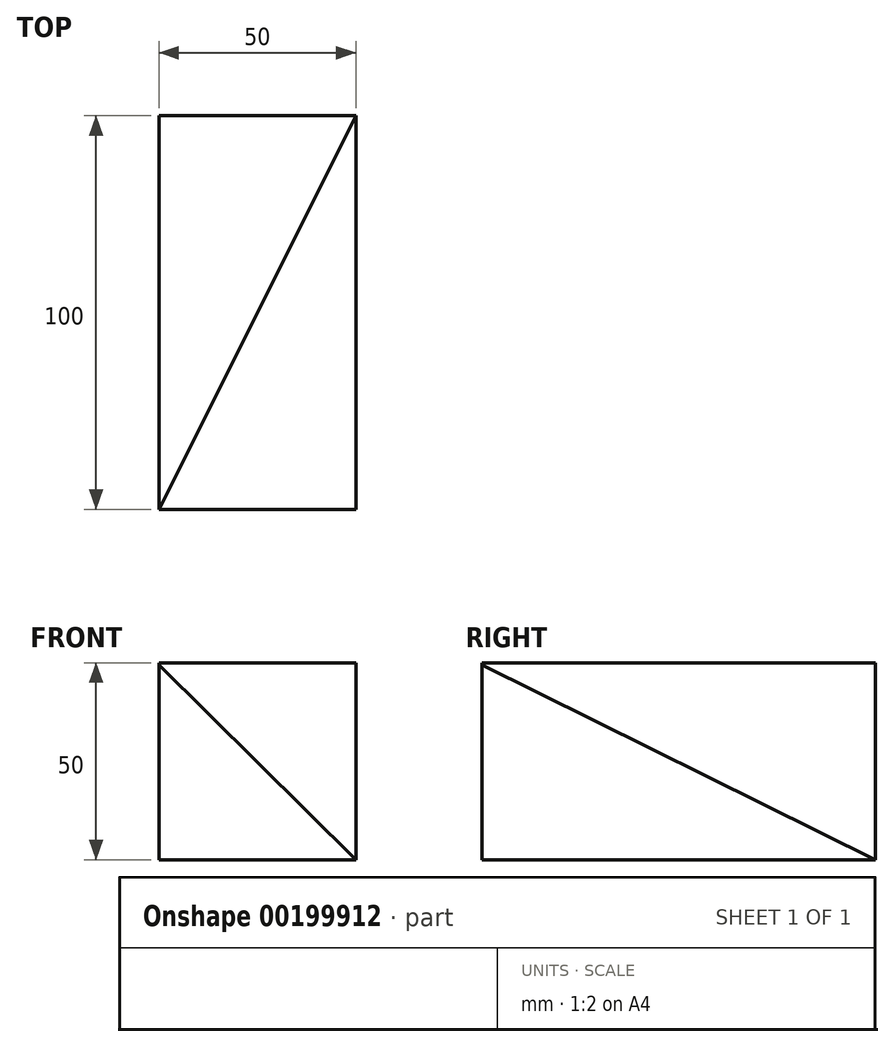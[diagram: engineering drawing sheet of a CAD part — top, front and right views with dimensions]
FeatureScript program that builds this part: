
annotation { "Feature Type Name" : "Feature", "Feature Type Description" : "" }
export const myFeature = defineFeature(function(context is Context, id is Id, definition is map)
    precondition{}
    {
        {
            var Q0;
            Q0=qCreatedBy(makeId("Top.planeOp"),FACE);
            var sketch = newSketch(context, id + "F0", { "sketchPlane" : qUnion([Q0])});
            skLineSegment(sketch, "E0", {"start": v(0, 0) * mm, "end": v(0, 100) * mm});
            skLineSegment(sketch, "E1", {"start": v(0, 100) * mm, "end": v(50, 100) * mm});
            skLineSegment(sketch, "E2", {"start": v(50, 100) * mm, "end": v(0, 0) * mm});
            skSolve(sketch);
        }
        {
            var Q0;
            Q0 = qSketchRegion(id + "F0", true);
            extrude(context, id + "F1", {"entities" : qUnion([Q0]), "depth" : 50 * mm});
        }
        {
            var Q0;
            Q0=qCreatedBy(makeId("Front.planeOp"),FACE);
            var sketch = newSketch(context, id + "F2", { "sketchPlane" : qUnion([Q0])});
            skLineSegment(sketch, "E3", {"start": v(0, 49.43) * mm, "end": v(0, 0) * mm});
            skLineSegment(sketch, "E4", {"start": v(0, 0) * mm, "end": v(50, 0) * mm});
            skLineSegment(sketch, "E5", {"start": v(50, 0) * mm, "end": v(0, 49.43) * mm});
            skSolve(sketch);
        }
        {
            var Q0;
            Q0=makeQuery(id+"F2.imprint","IMPRINT",FACE,{"disambiguationData":[TD([[makeQuery(id+"F2.imprint","IMPRINT",EDGE,{"derivedFrom":sQuery(id+"F2.wireOp",EDGE,"E3")}),1.0]])]});
            extrude(context, id + "F3", {"entities" : qUnion([Q0]), "operationType" : NewBodyOperationType.ADD, "oppositeDirection" : true, "depth" : 100 * mm});
        }
    });
